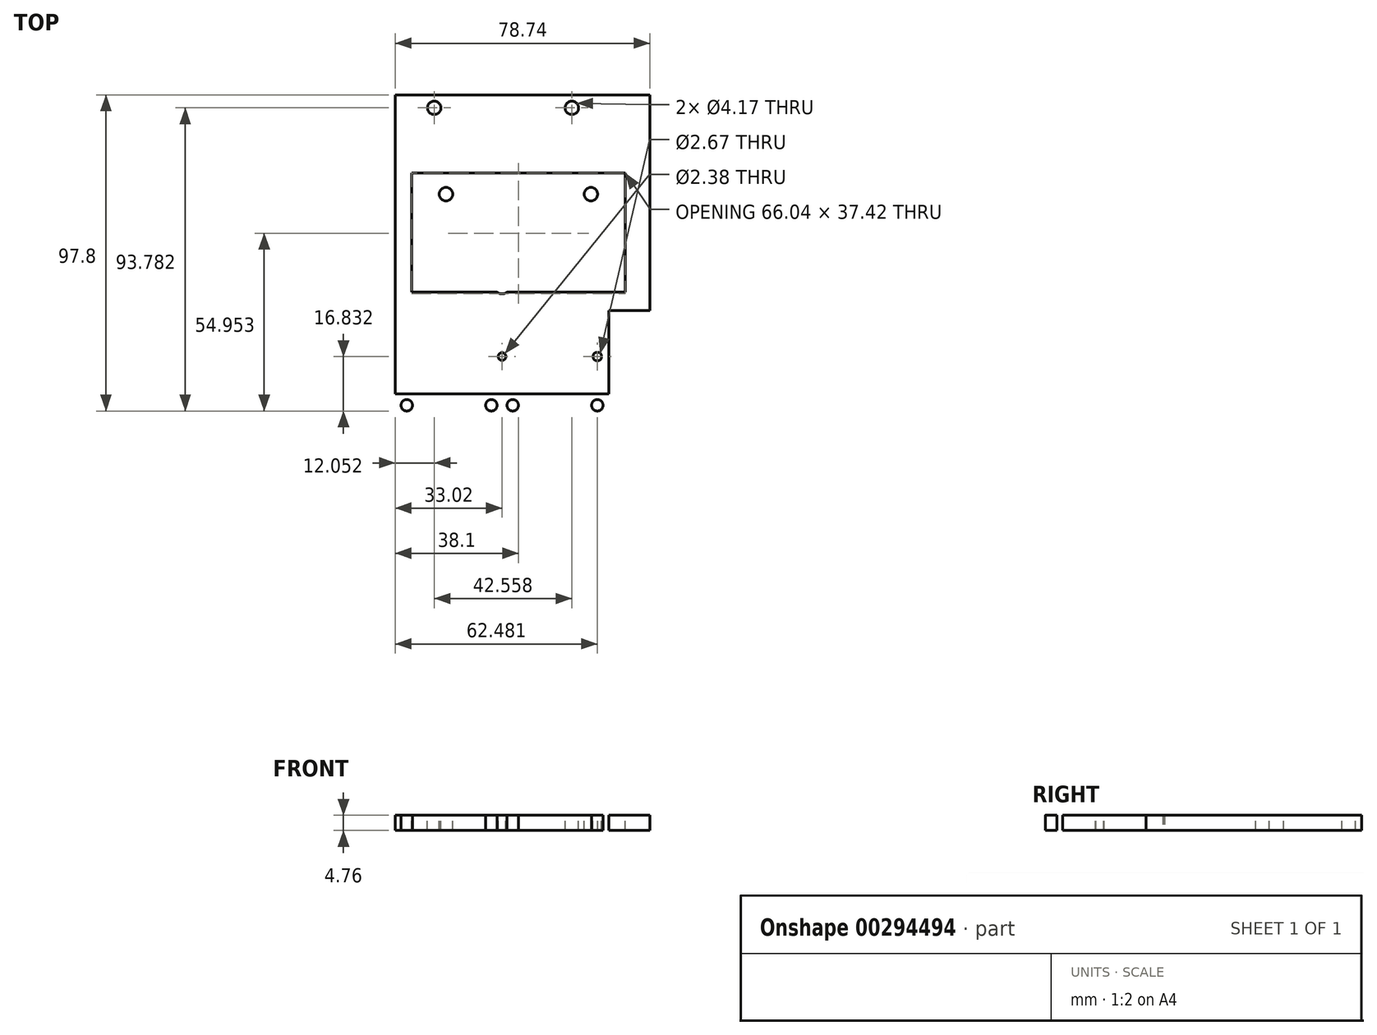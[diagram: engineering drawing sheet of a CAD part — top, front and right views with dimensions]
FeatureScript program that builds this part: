
annotation { "Feature Type Name" : "Feature", "Feature Type Description" : "" }
export const myFeature = defineFeature(function(context is Context, id is Id, definition is map)
    precondition{}
    {
        {
            var Q0;
            Q0=qCreatedBy(makeId("Top.planeOp"),FACE);
            var sketch = newSketch(context, id + "F0", { "sketchPlane" : qUnion([Q0])});
            skLineSegment(sketch, "E0.bottom", {"start": v(33.02, 53.98) * mm, "end": v(-33.02, 53.98) * mm});
            skLineSegment(sketch, "E0.top", {"start": v(33.02, -53.98) * mm, "end": v(-33.02, -53.98) * mm});
            skLineSegment(sketch, "E0.left", {"start": v(33.02, -12.7) * mm, "end": v(33.02, -53.98) * mm});
            skLineSegment(sketch, "E0.right", {"start": v(-33.02, 53.98) * mm, "end": v(-33.02, -53.98) * mm});
            skPoint(sketch, "E0.middle", {"position": v(0, 0) * mm});
            skLineSegment(sketch, "E1.bottom", {"start": v(33.02, 53.98) * mm, "end": v(45.72, 53.98) * mm});
            skLineSegment(sketch, "E1.top", {"start": v(33.02, -12.7) * mm, "end": v(45.72, -12.7) * mm});
            skLineSegment(sketch, "E1.right", {"start": v(45.72, 53.98) * mm, "end": v(45.72, -12.7) * mm});
            skSolve(sketch);
        }
        {
            var Q0;
            Q0=makeQuery(id+"F0.imprint","IMPRINT",FACE,{"disambiguationData":[TD([[makeQuery(id+"F0.imprint","IMPRINT",EDGE,{"derivedFrom":sQuery(id+"F0.wireOp",EDGE,"E0.bottom")}),1.0]])]});
            extrude(context, id + "F1", {"entities" : qUnion([Q0]), "depth" : 4.76 * mm});
        }
        {
            var Q0;
            Q0=makeQuery(id+"F1.opExtrude","CAP_FACE",FACE,{"disambiguationData":[OSD([sQuery(id+"F0.wireOp",EDGE,"E0.bottom"),sQuery(id+"F0.wireOp",EDGE,"E0.top"),sQuery(id+"F0.wireOp",EDGE,"E0.left"),sQuery(id+"F0.wireOp",EDGE,"E0.right")])],"isStart":false});
            var sketch = newSketch(context, id + "F2", { "sketchPlane" : qUnion([Q0])});
            skLineSegment(sketch, "E2.bottom", {"start": v(38.1, 29.85) * mm, "end": v(-27.94, 29.85) * mm});
            skLineSegment(sketch, "E2.top", {"start": v(38.1, -6.98) * mm, "end": v(-27.94, -6.98) * mm});
            skLineSegment(sketch, "E2.left", {"start": v(38.1, 29.85) * mm, "end": v(38.1, -6.98) * mm});
            skLineSegment(sketch, "E2.right", {"start": v(-27.94, 29.85) * mm, "end": v(-27.94, -6.98) * mm});
            skPoint(sketch, "E2.middle", {"position": v(5.08, 11.43) * mm});
            skLineSegment(sketch, "E3.bottom", {"start": v(27.48, 29.85) * mm, "end": v(-17.32, 29.85) * mm});
            skLineSegment(sketch, "E3.top", {"start": v(27.48, -6.98) * mm, "end": v(-17.32, -6.98) * mm});
            skLineSegment(sketch, "E3.left", {"start": v(27.48, 29.85) * mm, "end": v(27.48, -6.98) * mm});
            skLineSegment(sketch, "E3.right", {"start": v(-17.32, 29.85) * mm, "end": v(-17.32, -6.98) * mm});
            skCircle(sketch, "E4", {"center": v(27.48, 23.24) * mm, "radius": 2.08 * mm});
            skCircle(sketch, "E5", {"center": v(27.48, -2.92) * mm, "radius": 2.08 * mm});
            skCircle(sketch, "E6", {"center": v(-17.32, 23.24) * mm, "radius": 2.08 * mm});
            skCircle(sketch, "E7", {"center": v(-17.32, -2.92) * mm, "radius": 2.08 * mm});
            skLineSegment(sketch, "E8", {"start": v(-33.02, 31.67) * mm, "end": v(45.72, 31.67) * mm});
            skLineSegment(sketch, "E9.bottom", {"start": v(27.48, 31.67) * mm, "end": v(-17.26, 31.67) * mm});
            skLineSegment(sketch, "E9.top", {"start": v(27.48, 41.83) * mm, "end": v(-17.26, 41.83) * mm});
            skLineSegment(sketch, "E9.left", {"start": v(27.48, 31.67) * mm, "end": v(27.48, 41.83) * mm});
            skLineSegment(sketch, "E9.right", {"start": v(-17.26, 31.67) * mm, "end": v(-17.26, 41.83) * mm});
            skCircle(sketch, "E10", {"center": v(21.59, 49.96) * mm, "radius": 2.08 * mm});
            skCircle(sketch, "E11", {"center": v(-20.97, 49.96) * mm, "radius": 2.08 * mm});
            skLineSegment(sketch, "E12", {"start": v(-20.97, 49.96) * mm, "end": v(21.59, 49.96) * mm});
            skLineSegment(sketch, "E13", {"start": v(6.35, 53.98) * mm, "end": v(6.35, 11.43) * mm});
            skLineSegment(sketch, "E14", {"start": v(27.48, 41.83) * mm, "end": v(27.48, 53.98) * mm});
            skSolve(sketch);
        }
        {
            var Q0;
            {var subQ0=sQuery(id+"F2.wireOp",EDGE,"E6");var subQ1=sQuery(id+"F2.wireOp",EDGE,"E3.right");var subQ2=makeQuery(id+"F2.imprint","INTERSECT",VERTEX,{"disambiguationData":[OD(0.0)],"derivedFrom":[subQ1,subQ0]});Q0=makeQuery(id+"F2.imprint","IMPRINT",FACE,{"disambiguationData":[TD([[makeQuery(id+"F2.imprint","IMPRINT",EDGE,{"disambiguationData":[TD([[subQ2,-1.0]])],"derivedFrom":subQ1}),1.0]])]});}
            var Q1;
            {var subQ0=sQuery(id+"F2.wireOp",EDGE,"E6");var subQ1=sQuery(id+"F2.wireOp",EDGE,"E3.right");var subQ2=makeQuery(id+"F2.imprint","INTERSECT",VERTEX,{"disambiguationData":[OD(0.0)],"derivedFrom":[subQ1,subQ0]});Q1=makeQuery(id+"F2.imprint","IMPRINT",FACE,{"disambiguationData":[TD([[makeQuery(id+"F2.imprint","IMPRINT",EDGE,{"disambiguationData":[TD([[subQ2,-1.0]])],"derivedFrom":subQ1}),-1.0]])]});}
            var Q2;
            {var subQ0=sQuery(id+"F2.wireOp",EDGE,"E7");var subQ1=sQuery(id+"F2.wireOp",EDGE,"E3.right");var subQ2=makeQuery(id+"F2.imprint","INTERSECT",VERTEX,{"disambiguationData":[OD(0.0)],"derivedFrom":[subQ1,subQ0]});Q2=makeQuery(id+"F2.imprint","IMPRINT",FACE,{"disambiguationData":[TD([[makeQuery(id+"F2.imprint","IMPRINT",EDGE,{"disambiguationData":[TD([[subQ2,-1.0]])],"derivedFrom":subQ1}),1.0]])]});}
            var Q3;
            {var subQ0=sQuery(id+"F2.wireOp",EDGE,"E7");var subQ1=sQuery(id+"F2.wireOp",EDGE,"E3.right");var subQ2=makeQuery(id+"F2.imprint","INTERSECT",VERTEX,{"disambiguationData":[OD(0.0)],"derivedFrom":[subQ1,subQ0]});Q3=makeQuery(id+"F2.imprint","IMPRINT",FACE,{"disambiguationData":[TD([[makeQuery(id+"F2.imprint","IMPRINT",EDGE,{"disambiguationData":[TD([[subQ2,-1.0]])],"derivedFrom":subQ1}),-1.0]])]});}
            var Q4;
            {var subQ0=sQuery(id+"F2.wireOp",EDGE,"E5");var subQ1=sQuery(id+"F2.wireOp",EDGE,"E3.left");var subQ2=makeQuery(id+"F2.imprint","INTERSECT",VERTEX,{"disambiguationData":[OD(0.0)],"derivedFrom":[subQ1,subQ0]});Q4=makeQuery(id+"F2.imprint","IMPRINT",FACE,{"disambiguationData":[TD([[makeQuery(id+"F2.imprint","IMPRINT",EDGE,{"disambiguationData":[TD([[subQ2,-1.0]])],"derivedFrom":subQ1}),-1.0]])]});}
            var Q5;
            {var subQ0=sQuery(id+"F2.wireOp",EDGE,"E5");var subQ1=sQuery(id+"F2.wireOp",EDGE,"E3.left");var subQ2=makeQuery(id+"F2.imprint","INTERSECT",VERTEX,{"disambiguationData":[OD(0.0)],"derivedFrom":[subQ1,subQ0]});Q5=makeQuery(id+"F2.imprint","IMPRINT",FACE,{"disambiguationData":[TD([[makeQuery(id+"F2.imprint","IMPRINT",EDGE,{"disambiguationData":[TD([[subQ2,-1.0]])],"derivedFrom":subQ1}),1.0]])]});}
            var Q6;
            {var subQ0=sQuery(id+"F2.wireOp",EDGE,"E4");var subQ1=sQuery(id+"F2.wireOp",EDGE,"E3.left");var subQ2=makeQuery(id+"F2.imprint","INTERSECT",VERTEX,{"disambiguationData":[OD(0.0)],"derivedFrom":[subQ1,subQ0]});Q6=makeQuery(id+"F2.imprint","IMPRINT",FACE,{"disambiguationData":[TD([[makeQuery(id+"F2.imprint","IMPRINT",EDGE,{"disambiguationData":[TD([[subQ2,-1.0]])],"derivedFrom":subQ1}),1.0]])]});}
            var Q7;
            {var subQ0=sQuery(id+"F2.wireOp",EDGE,"E4");var subQ1=sQuery(id+"F2.wireOp",EDGE,"E3.left");var subQ2=makeQuery(id+"F2.imprint","INTERSECT",VERTEX,{"disambiguationData":[OD(0.0)],"derivedFrom":[subQ1,subQ0]});Q7=makeQuery(id+"F2.imprint","IMPRINT",FACE,{"disambiguationData":[TD([[makeQuery(id+"F2.imprint","IMPRINT",EDGE,{"disambiguationData":[TD([[subQ2,-1.0]])],"derivedFrom":subQ1}),-1.0]])]});}
            extrude(context, id + "F3", {"entities" : qUnion([Q0, Q1, Q2, Q3, Q4, Q5, Q6, Q7]), "operationType" : NewBodyOperationType.REMOVE, "oppositeDirection" : true, "depth" : 25.4 * mm});
        }
        {
            var Q0;
            Q0=makeQuery(id+"F1.opExtrude","CAP_FACE",FACE,{"disambiguationData":[OSD([sQuery(id+"F0.wireOp",EDGE,"E0.bottom"),sQuery(id+"F0.wireOp",EDGE,"E0.top"),sQuery(id+"F0.wireOp",EDGE,"E0.left"),sQuery(id+"F0.wireOp",EDGE,"E0.right"),sQuery(id+"F0.wireOp",EDGE,"E1.bottom"),sQuery(id+"F0.wireOp",EDGE,"E1.top"),sQuery(id+"F0.wireOp",EDGE,"E1.right")])],"isStart":true});
            var sketch = newSketch(context, id + "F4", { "sketchPlane" : qUnion([Q0])});
            skCircle(sketch, "E15", {"center": v(0, 5.08) * mm, "radius": 2.5 * mm});
            skSolve(sketch);
        }
        {
            var Q0;
            Q0=makeQuery(id+"F4.imprint","IMPRINT",FACE,{"disambiguationData":[TD([[makeQuery(id+"F4.imprint","IMPRINT",EDGE,{"derivedFrom":sQuery(id+"F4.wireOp",EDGE,"E15")}),1.0]])]});
            extrude(context, id + "F5", {"entities" : qUnion([Q0]), "operationType" : NewBodyOperationType.REMOVE, "oppositeDirection" : true, "depth" : 25.4 * mm});
        }
        {
            var Q0;
            Q0=makeQuery(id+"F1.opExtrude","CAP_FACE",FACE,{"disambiguationData":[OSD([sQuery(id+"F0.wireOp",EDGE,"E0.bottom"),sQuery(id+"F0.wireOp",EDGE,"E0.top"),sQuery(id+"F0.wireOp",EDGE,"E0.left"),sQuery(id+"F0.wireOp",EDGE,"E0.right"),sQuery(id+"F0.wireOp",EDGE,"E1.bottom"),sQuery(id+"F0.wireOp",EDGE,"E1.top"),sQuery(id+"F0.wireOp",EDGE,"E1.right")])],"isStart":false});
            var sketch = newSketch(context, id + "F6", { "sketchPlane" : qUnion([Q0])});
            skCircle(sketch, "E16", {"center": v(0, -26.99) * mm, "radius": 1.2 * mm});
            skLineSegment(sketch, "E17", {"start": v(0, 0) * mm, "end": v(0, -53.98) * mm});
            skCircle(sketch, "E18", {"center": v(29.46, -26.99) * mm, "radius": 1.33 * mm});
            skSolve(sketch);
        }
        {
            var Q0;
            Q0=makeQuery(id+"F6.imprint","IMPRINT",FACE,{"disambiguationData":[TD([[makeQuery(id+"F6.imprint","IMPRINT",EDGE,{"derivedFrom":sQuery(id+"F6.wireOp",EDGE,"JMl9nRko-QcrZ-EN4P-RaXr-sKlmFHKYxudj")}),1.0]])]});
            var Q1;
            Q1=makeQuery(id+"F6.imprint","IMPRINT",FACE,{"disambiguationData":[TD([[makeQuery(id+"F6.imprint","IMPRINT",EDGE,{"derivedFrom":sQuery(id+"F6.wireOp",EDGE,"E16")}),1.0]])]});
            var Q2;
            Q2=makeQuery(id+"F6.imprint","IMPRINT",FACE,{"disambiguationData":[TD([[makeQuery(id+"F6.imprint","IMPRINT",EDGE,{"derivedFrom":sQuery(id+"F6.wireOp",EDGE,"E18")}),1.0]])]});
            extrude(context, id + "F7", {"entities" : qUnion([Q0, Q1, Q2]), "operationType" : NewBodyOperationType.REMOVE, "oppositeDirection" : true, "depth" : 25.4 * mm});
        }
        {
            var Q0;
            Q0=makeQuery(id+"F2.imprint","IMPRINT",FACE,{"disambiguationData":[TD([[makeQuery(id+"F2.imprint","IMPRINT",EDGE,{"derivedFrom":sQuery(id+"F2.wireOp",EDGE,"E9.bottom")}),-1.0]])]});
            var Q1;
            Q1=makeQuery(id+"F2.imprint","IMPRINT",FACE,{"disambiguationData":[TD([[makeQuery(id+"F2.imprint","IMPRINT",EDGE,{"derivedFrom":sQuery(id+"F2.wireOp",EDGE,"E11")}),1.0]])]});
            var Q2;
            Q2=makeQuery(id+"F2.imprint","IMPRINT",FACE,{"disambiguationData":[TD([[makeQuery(id+"F2.imprint","IMPRINT",EDGE,{"derivedFrom":sQuery(id+"F2.wireOp",EDGE,"E10")}),1.0]])]});
            extrude(context, id + "F8", {"entities" : qUnion([Q0, Q1, Q2]), "operationType" : NewBodyOperationType.REMOVE, "oppositeDirection" : true, "depth" : 25.4 * mm});
        }
        {
            var Q0;
            Q0=makeQuery(id+"F1.opExtrude","CAP_FACE",FACE,{"disambiguationData":[OSD([sQuery(id+"F0.wireOp",EDGE,"E0.bottom"),sQuery(id+"F0.wireOp",EDGE,"E0.top"),sQuery(id+"F0.wireOp",EDGE,"E0.left"),sQuery(id+"F0.wireOp",EDGE,"E0.right"),sQuery(id+"F0.wireOp",EDGE,"E1.bottom"),sQuery(id+"F0.wireOp",EDGE,"E1.top"),sQuery(id+"F0.wireOp",EDGE,"E1.right")])],"isStart":false});
            var sketch = newSketch(context, id + "F9", { "sketchPlane" : qUnion([Q0])});
            skLineSegment(sketch, "E19.bottom", {"start": v(33.02, -38.48) * mm, "end": v(-33.02, -38.48) * mm});
            skLineSegment(sketch, "E19.top", {"start": v(33.02, -53.98) * mm, "end": v(-33.02, -53.98) * mm});
            skLineSegment(sketch, "E19.left", {"start": v(33.02, -38.48) * mm, "end": v(33.02, -53.97) * mm});
            skLineSegment(sketch, "E19.right", {"start": v(-33.02, -38.48) * mm, "end": v(-33.02, -53.98) * mm});
            skPoint(sketch, "E19.middle", {"position": v(0, -46.23) * mm});
            skLineSegment(sketch, "E20", {"start": v(-3.3, -38.48) * mm, "end": v(-3.3, -53.98) * mm});
            skLineSegment(sketch, "E21", {"start": v(3.3, -38.48) * mm, "end": v(3.3, -53.98) * mm});
            skCircle(sketch, "E22", {"center": v(3.3, -50.33) * mm, "radius": 1.78 * mm});
            skCircle(sketch, "E23", {"center": v(3.3, -42.05) * mm, "radius": 1.78 * mm});
            skCircle(sketch, "E24", {"center": v(-3.3, -42.05) * mm, "radius": 1.78 * mm});
            skCircle(sketch, "E25", {"center": v(-3.3, -50.33) * mm, "radius": 1.78 * mm});
            skLineSegment(sketch, "E26", {"start": v(29.46, -38.48) * mm, "end": v(29.46, -53.97) * mm});
            skLineSegment(sketch, "E27", {"start": v(-29.46, -38.48) * mm, "end": v(-29.46, -53.98) * mm});
            skCircle(sketch, "E28", {"center": v(29.46, -42.05) * mm, "radius": 1.78 * mm});
            skCircle(sketch, "E29", {"center": v(29.46, -50.33) * mm, "radius": 1.78 * mm});
            skCircle(sketch, "E30", {"center": v(-29.46, -50.33) * mm, "radius": 1.78 * mm});
            skCircle(sketch, "E31", {"center": v(-29.46, -42.05) * mm, "radius": 1.78 * mm});
            skSolve(sketch);
        }
        {
            var Q0;
            {var subQ0=sQuery(id+"F9.wireOp",EDGE,"E30");var subQ1=sQuery(id+"F9.wireOp",EDGE,"E27");var subQ2=makeQuery(id+"F9.imprint","INTERSECT",VERTEX,{"disambiguationData":[OD(0.0)],"derivedFrom":[subQ1,subQ0]});Q0=makeQuery(id+"F9.imprint","IMPRINT",FACE,{"disambiguationData":[TD([[makeQuery(id+"F9.imprint","IMPRINT",EDGE,{"disambiguationData":[TD([[subQ2,-1.0]])],"derivedFrom":subQ1}),1.0]])]});}
            var Q1;
            {var subQ0=sQuery(id+"F9.wireOp",EDGE,"E30");var subQ1=sQuery(id+"F9.wireOp",EDGE,"E27");var subQ2=makeQuery(id+"F9.imprint","INTERSECT",VERTEX,{"disambiguationData":[OD(0.0)],"derivedFrom":[subQ1,subQ0]});Q1=makeQuery(id+"F9.imprint","IMPRINT",FACE,{"disambiguationData":[TD([[makeQuery(id+"F9.imprint","IMPRINT",EDGE,{"disambiguationData":[TD([[subQ2,-1.0]])],"derivedFrom":subQ1}),-1.0]])]});}
            var Q2;
            {var subQ0=sQuery(id+"F9.wireOp",EDGE,"E31");var subQ1=sQuery(id+"F9.wireOp",EDGE,"E27");var subQ2=makeQuery(id+"F9.imprint","INTERSECT",VERTEX,{"disambiguationData":[OD(0.0)],"derivedFrom":[subQ1,subQ0]});Q2=makeQuery(id+"F9.imprint","IMPRINT",FACE,{"disambiguationData":[TD([[makeQuery(id+"F9.imprint","IMPRINT",EDGE,{"disambiguationData":[TD([[subQ2,-1.0]])],"derivedFrom":subQ1}),1.0]])]});}
            var Q3;
            {var subQ0=sQuery(id+"F9.wireOp",EDGE,"E31");var subQ1=sQuery(id+"F9.wireOp",EDGE,"E27");var subQ2=makeQuery(id+"F9.imprint","INTERSECT",VERTEX,{"disambiguationData":[OD(0.0)],"derivedFrom":[subQ1,subQ0]});Q3=makeQuery(id+"F9.imprint","IMPRINT",FACE,{"disambiguationData":[TD([[makeQuery(id+"F9.imprint","IMPRINT",EDGE,{"disambiguationData":[TD([[subQ2,-1.0]])],"derivedFrom":subQ1}),-1.0]])]});}
            var Q4;
            {var subQ0=sQuery(id+"F9.wireOp",EDGE,"E24");var subQ1=sQuery(id+"F9.wireOp",EDGE,"E20");var subQ2=makeQuery(id+"F9.imprint","INTERSECT",VERTEX,{"disambiguationData":[OD(0.0)],"derivedFrom":[subQ1,subQ0]});Q4=makeQuery(id+"F9.imprint","IMPRINT",FACE,{"disambiguationData":[TD([[makeQuery(id+"F9.imprint","IMPRINT",EDGE,{"disambiguationData":[TD([[subQ2,-1.0]])],"derivedFrom":subQ1}),-1.0]])]});}
            var Q5;
            {var subQ0=sQuery(id+"F9.wireOp",EDGE,"E24");var subQ1=sQuery(id+"F9.wireOp",EDGE,"E20");var subQ2=makeQuery(id+"F9.imprint","INTERSECT",VERTEX,{"disambiguationData":[OD(0.0)],"derivedFrom":[subQ1,subQ0]});Q5=makeQuery(id+"F9.imprint","IMPRINT",FACE,{"disambiguationData":[TD([[makeQuery(id+"F9.imprint","IMPRINT",EDGE,{"disambiguationData":[TD([[subQ2,-1.0]])],"derivedFrom":subQ1}),1.0]])]});}
            var Q6;
            {var subQ0=sQuery(id+"F9.wireOp",EDGE,"E25");var subQ1=sQuery(id+"F9.wireOp",EDGE,"E20");var subQ2=makeQuery(id+"F9.imprint","INTERSECT",VERTEX,{"disambiguationData":[OD(0.0)],"derivedFrom":[subQ1,subQ0]});Q6=makeQuery(id+"F9.imprint","IMPRINT",FACE,{"disambiguationData":[TD([[makeQuery(id+"F9.imprint","IMPRINT",EDGE,{"disambiguationData":[TD([[subQ2,-1.0]])],"derivedFrom":subQ1}),-1.0]])]});}
            var Q7;
            {var subQ0=sQuery(id+"F9.wireOp",EDGE,"E25");var subQ1=sQuery(id+"F9.wireOp",EDGE,"E20");var subQ2=makeQuery(id+"F9.imprint","INTERSECT",VERTEX,{"disambiguationData":[OD(0.0)],"derivedFrom":[subQ1,subQ0]});Q7=makeQuery(id+"F9.imprint","IMPRINT",FACE,{"disambiguationData":[TD([[makeQuery(id+"F9.imprint","IMPRINT",EDGE,{"disambiguationData":[TD([[subQ2,-1.0]])],"derivedFrom":subQ1}),1.0]])]});}
            var Q8;
            {var subQ0=sQuery(id+"F9.wireOp",EDGE,"E22");var subQ1=sQuery(id+"F9.wireOp",EDGE,"E21");var subQ2=makeQuery(id+"F9.imprint","INTERSECT",VERTEX,{"disambiguationData":[OD(0.0)],"derivedFrom":[subQ1,subQ0]});Q8=makeQuery(id+"F9.imprint","IMPRINT",FACE,{"disambiguationData":[TD([[makeQuery(id+"F9.imprint","IMPRINT",EDGE,{"disambiguationData":[TD([[subQ2,-1.0]])],"derivedFrom":subQ1}),-1.0]])]});}
            var Q9;
            {var subQ0=sQuery(id+"F9.wireOp",EDGE,"E22");var subQ1=sQuery(id+"F9.wireOp",EDGE,"E21");var subQ2=makeQuery(id+"F9.imprint","INTERSECT",VERTEX,{"disambiguationData":[OD(0.0)],"derivedFrom":[subQ1,subQ0]});Q9=makeQuery(id+"F9.imprint","IMPRINT",FACE,{"disambiguationData":[TD([[makeQuery(id+"F9.imprint","IMPRINT",EDGE,{"disambiguationData":[TD([[subQ2,-1.0]])],"derivedFrom":subQ1}),1.0]])]});}
            var Q10;
            {var subQ0=sQuery(id+"F9.wireOp",EDGE,"E23");var subQ1=sQuery(id+"F9.wireOp",EDGE,"E21");var subQ2=makeQuery(id+"F9.imprint","INTERSECT",VERTEX,{"disambiguationData":[OD(0.0)],"derivedFrom":[subQ1,subQ0]});Q10=makeQuery(id+"F9.imprint","IMPRINT",FACE,{"disambiguationData":[TD([[makeQuery(id+"F9.imprint","IMPRINT",EDGE,{"disambiguationData":[TD([[subQ2,-1.0]])],"derivedFrom":subQ1}),1.0]])]});}
            var Q11;
            {var subQ0=sQuery(id+"F9.wireOp",EDGE,"E23");var subQ1=sQuery(id+"F9.wireOp",EDGE,"E21");var subQ2=makeQuery(id+"F9.imprint","INTERSECT",VERTEX,{"disambiguationData":[OD(0.0)],"derivedFrom":[subQ1,subQ0]});Q11=makeQuery(id+"F9.imprint","IMPRINT",FACE,{"disambiguationData":[TD([[makeQuery(id+"F9.imprint","IMPRINT",EDGE,{"disambiguationData":[TD([[subQ2,-1.0]])],"derivedFrom":subQ1}),-1.0]])]});}
            var Q12;
            {var subQ0=sQuery(id+"F9.wireOp",EDGE,"E28");var subQ1=sQuery(id+"F9.wireOp",EDGE,"E26");var subQ2=makeQuery(id+"F9.imprint","INTERSECT",VERTEX,{"disambiguationData":[OD(0.0)],"derivedFrom":[subQ1,subQ0]});Q12=makeQuery(id+"F9.imprint","IMPRINT",FACE,{"disambiguationData":[TD([[makeQuery(id+"F9.imprint","IMPRINT",EDGE,{"disambiguationData":[TD([[subQ2,-1.0]])],"derivedFrom":subQ1}),-1.0]])]});}
            var Q13;
            {var subQ0=sQuery(id+"F9.wireOp",EDGE,"E28");var subQ1=sQuery(id+"F9.wireOp",EDGE,"E26");var subQ2=makeQuery(id+"F9.imprint","INTERSECT",VERTEX,{"disambiguationData":[OD(0.0)],"derivedFrom":[subQ1,subQ0]});Q13=makeQuery(id+"F9.imprint","IMPRINT",FACE,{"disambiguationData":[TD([[makeQuery(id+"F9.imprint","IMPRINT",EDGE,{"disambiguationData":[TD([[subQ2,-1.0]])],"derivedFrom":subQ1}),1.0]])]});}
            var Q14;
            {var subQ0=sQuery(id+"F9.wireOp",EDGE,"E29");var subQ1=sQuery(id+"F9.wireOp",EDGE,"E26");var subQ2=makeQuery(id+"F9.imprint","INTERSECT",VERTEX,{"disambiguationData":[OD(0.0)],"derivedFrom":[subQ1,subQ0]});Q14=makeQuery(id+"F9.imprint","IMPRINT",FACE,{"disambiguationData":[TD([[makeQuery(id+"F9.imprint","IMPRINT",EDGE,{"disambiguationData":[TD([[subQ2,-1.0]])],"derivedFrom":subQ1}),1.0]])]});}
            var Q15;
            {var subQ0=sQuery(id+"F9.wireOp",EDGE,"E29");var subQ1=sQuery(id+"F9.wireOp",EDGE,"E26");var subQ2=makeQuery(id+"F9.imprint","INTERSECT",VERTEX,{"disambiguationData":[OD(0.0)],"derivedFrom":[subQ1,subQ0]});Q15=makeQuery(id+"F9.imprint","IMPRINT",FACE,{"disambiguationData":[TD([[makeQuery(id+"F9.imprint","IMPRINT",EDGE,{"disambiguationData":[TD([[subQ2,-1.0]])],"derivedFrom":subQ1}),-1.0]])]});}
            extrude(context, id + "F10", {"entities" : qUnion([Q0, Q1, Q2, Q3, Q4, Q5, Q6, Q7, Q8, Q9, Q10, Q11, Q12, Q13, Q14, Q15]), "operationType" : NewBodyOperationType.REMOVE, "oppositeDirection" : true, "depth" : 25.4 * mm});
        }
    });
